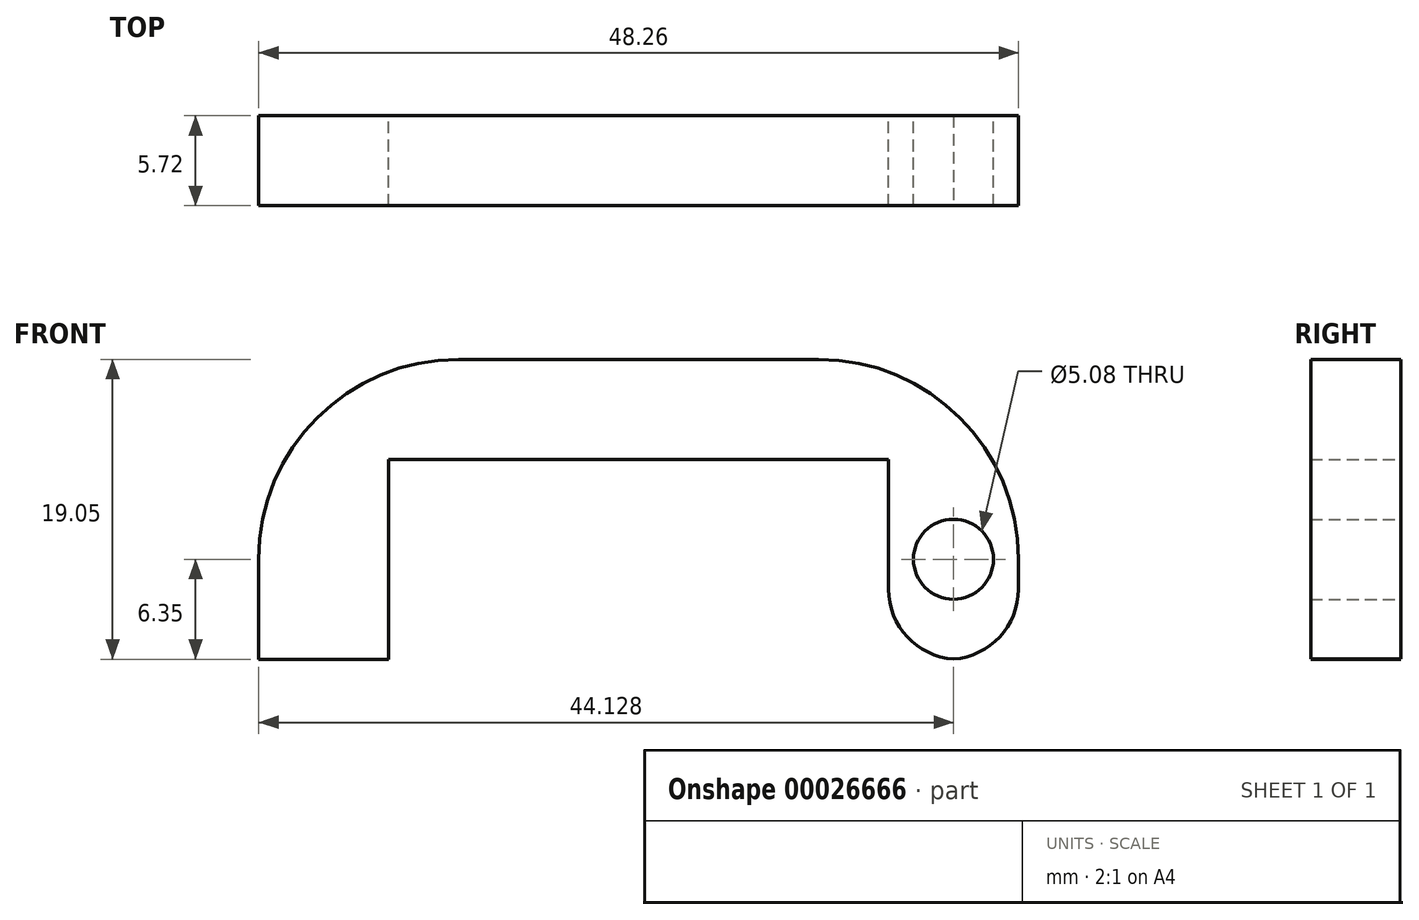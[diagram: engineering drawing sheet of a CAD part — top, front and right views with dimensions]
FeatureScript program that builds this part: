
annotation { "Feature Type Name" : "Feature", "Feature Type Description" : "" }
export const myFeature = defineFeature(function(context is Context, id is Id, definition is map)
    precondition{}
    {
        {
            var Q0;
            Q0=qCreatedBy(makeId("Front.planeOp"),FACE);
            var sketch = newSketch(context, id + "F0", { "sketchPlane" : qUnion([Q0])});
            skLineSegment(sketch, "E0", {"start": v(14.5, -41.72) * mm, "end": v(22.75, -41.72) * mm});
            skLineSegment(sketch, "E1", {"start": v(22.75, -41.72) * mm, "end": v(22.75, -22.67) * mm});
            skLineSegment(sketch, "E2", {"start": v(14.5, -41.72) * mm, "end": v(14.5, -29.02) * mm});
            skLineSegment(sketch, "E3", {"start": v(14.5, -29.02) * mm, "end": v(-17.26, -29.02) * mm});
            skLineSegment(sketch, "E4", {"start": v(-17.26, -29.02) * mm, "end": v(-17.26, -41.72) * mm});
            skLineSegment(sketch, "E5", {"start": v(-25.51, -22.67) * mm, "end": v(-25.51, -41.72) * mm});
            skLineSegment(sketch, "E6", {"start": v(-17.26, -41.72) * mm, "end": v(-25.51, -41.72) * mm});
            skLineSegment(sketch, "E7", {"start": v(-25.51, -22.67) * mm, "end": v(22.75, -22.67) * mm});
            skLineSegment(sketch, "E8", {"start": v(14.5, -35.37) * mm, "end": v(22.75, -35.37) * mm});
            skLineSegment(sketch, "E9", {"start": v(18.62, -41.72) * mm, "end": v(18.62, -35.37) * mm});
            skCircle(sketch, "E10", {"center": v(18.62, -35.37) * mm, "radius": 2.54 * mm});
            skLineSegment(sketch, "E11", {"start": v(-25.51, -41.72) * mm, "end": v(-25.51, -22.67) * mm});
            skSolve(sketch);
        }
        {
            var Q0;
            {var subQ9=sQuery(id+"F0.wireOp",EDGE,"E3");Q0=makeQuery(id+"F0.imprint","IMPRINT",FACE,{"disambiguationData":[TD([[makeQuery(id+"F0.imprint","IMPRINT",EDGE,{"derivedFrom":subQ9}),-1.0]])]});}
            var Q1;
            {var subQ3=sQuery(id+"F0.wireOp",EDGE,"E0");var subQ7=sQuery(id+"F0.wireOp",EDGE,"E2");var subQ9=makeQuery(id+"F0.imprint","INTERSECT",VERTEX,{"derivedFrom":[subQ3,subQ7]});Q1=makeQuery(id+"F0.imprint","IMPRINT",FACE,{"disambiguationData":[TD([[makeQuery(id+"F0.imprint","IMPRINT",EDGE,{"disambiguationData":[TD([[subQ9,-1.0]])],"derivedFrom":subQ3}),1.0]])]});}
            var Q2;
            {var subQ5=sQuery(id+"F0.wireOp",EDGE,"E0");var subQ7=sQuery(id+"F0.wireOp",EDGE,"E1");var subQ9=makeQuery(id+"F0.imprint","INTERSECT",VERTEX,{"derivedFrom":[subQ5,subQ7]});Q2=makeQuery(id+"F0.imprint","IMPRINT",FACE,{"disambiguationData":[TD([[makeQuery(id+"F0.imprint","IMPRINT",EDGE,{"disambiguationData":[TD([[subQ9,1.0]])],"derivedFrom":subQ5}),1.0]])]});}
            extrude(context, id + "F1", {"entities" : qUnion([Q0, Q1, Q2]), "depth" : 5.7 * mm});
        }
        {
            var Q0;
            Q0=makeQuery(id+"F1.opExtrude","SWEPT_EDGE",EDGE,{"disambiguationData":[OSD([sQuery(id+"F0.wireOp",EDGE,"E1"),sQuery(id+"F0.wireOp",EDGE,"E7")])]});
            var Q1;
            Q1=makeQuery(id+"F1.opExtrude","SWEPT_EDGE",EDGE,{"disambiguationData":[OSD([sQuery(id+"F0.wireOp",EDGE,"E7"),sQuery(id+"F0.wireOp",EDGE,"E11")])]});
            fillet(context, id + "F2", {"entities" : qUnion([Q0, Q1]), "radius" : 12.7 * mm, "tangentPropagation" : true, "allowEdgeOverflow" : false});
        }
        {
            var Q0;
            Q0=makeQuery(id+"F1.opExtrude","SWEPT_EDGE",EDGE,{"disambiguationData":[OSD([sQuery(id+"F0.wireOp",EDGE,"E0"),sQuery(id+"F0.wireOp",EDGE,"E2")])]});
            var Q1;
            Q1=makeQuery(id+"F1.opExtrude","SWEPT_EDGE",EDGE,{"disambiguationData":[OSD([sQuery(id+"F0.wireOp",EDGE,"E0"),sQuery(id+"F0.wireOp",EDGE,"E1")])]});
            fillet(context, id + "F3", {"entities" : qUnion([Q0, Q1]), "radius" : 4.44 * mm, "tangentPropagation" : true, "allowEdgeOverflow" : false});
        }
    });
